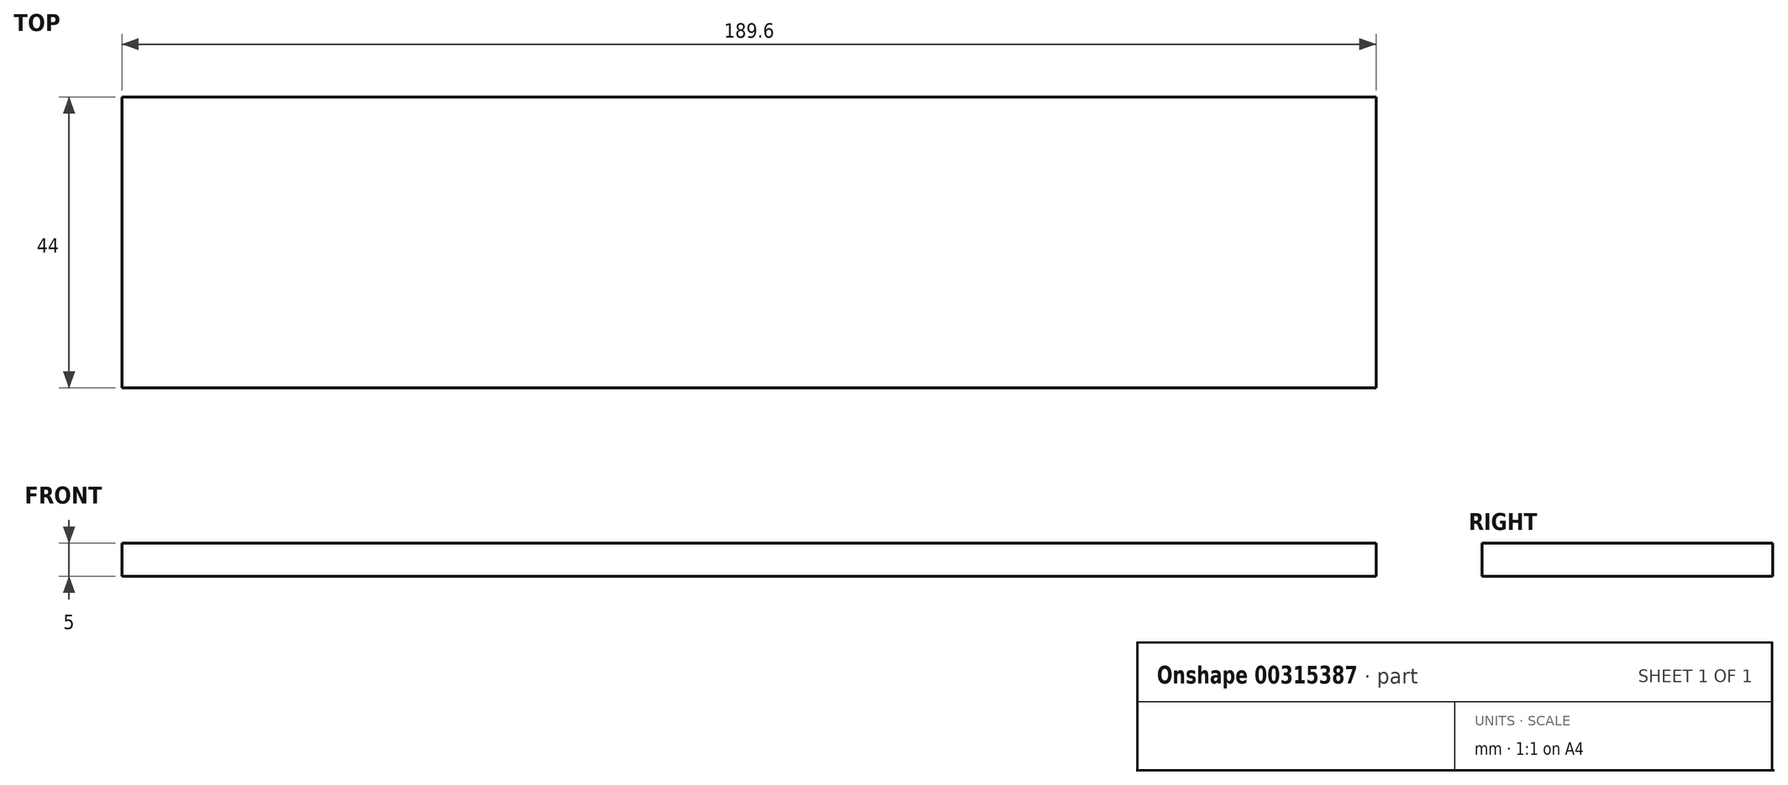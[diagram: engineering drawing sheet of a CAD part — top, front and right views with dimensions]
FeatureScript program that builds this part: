
annotation { "Feature Type Name" : "Feature", "Feature Type Description" : "" }
export const myFeature = defineFeature(function(context is Context, id is Id, definition is map)
    precondition{}
    {
        {
            var Q0;
            Q0=qCreatedBy(makeId("Top.planeOp"),FACE);
            var sketch = newSketch(context, id + "F0", { "sketchPlane" : qUnion([Q0])});
            skLineSegment(sketch, "E0.bottom", {"start": v(-94.8, 22) * mm, "end": v(94.8, 22) * mm});
            skLineSegment(sketch, "E0.top", {"start": v(-94.8, -22) * mm, "end": v(94.8, -22) * mm});
            skLineSegment(sketch, "E0.left", {"start": v(-94.8, 22) * mm, "end": v(-94.8, -22) * mm});
            skLineSegment(sketch, "E0.right", {"start": v(94.8, 22) * mm, "end": v(94.8, -22) * mm});
            skPoint(sketch, "E0.middle", {"position": v(0, 0) * mm});
            skSolve(sketch);
        }
        {
            var Q0;
            Q0=makeQuery(id+"F0.imprint","IMPRINT",FACE,{"disambiguationData":[TD([[makeQuery(id+"F0.imprint","IMPRINT",EDGE,{"derivedFrom":sQuery(id+"F0.wireOp",EDGE,"E0.bottom")}),-1.0]])]});
            extrude(context, id + "F1", {"entities" : qUnion([Q0]), "depth" : 5 * mm});
        }
    });
